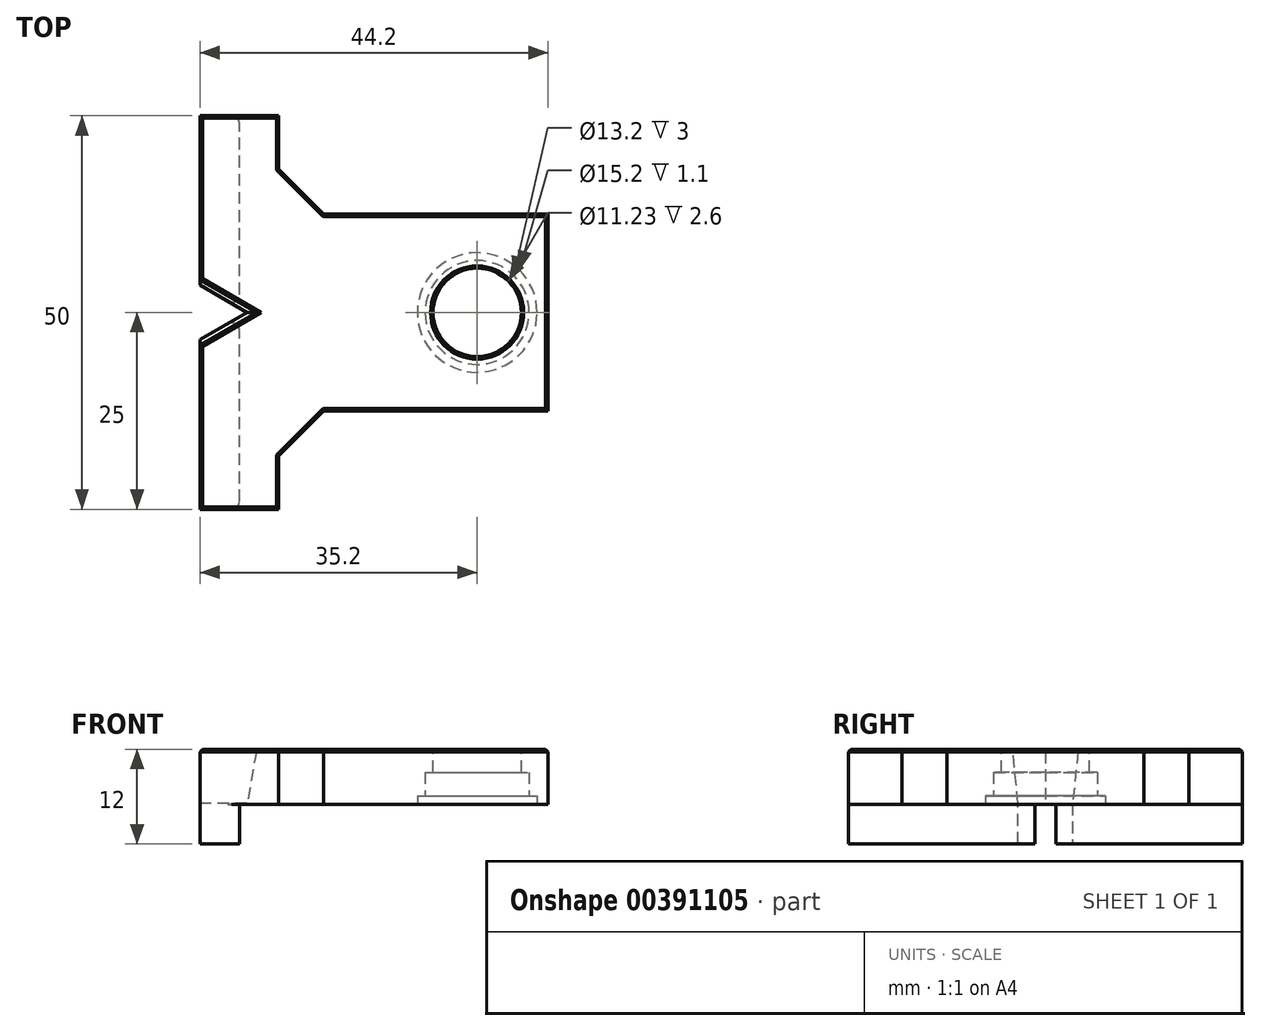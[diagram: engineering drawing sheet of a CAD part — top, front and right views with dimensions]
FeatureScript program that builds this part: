
annotation { "Feature Type Name" : "Feature", "Feature Type Description" : "" }
export const myFeature = defineFeature(function(context is Context, id is Id, definition is map)
    precondition{}
    {
        {
            var Q0;
            Q0=qCreatedBy(makeId("Front.planeOp"),FACE);
            var sketch = newSketch(context, id + "F0", { "sketchPlane" : qUnion([Q0])});
            skLineSegment(sketch, "E0", {"start": v(0, 4) * mm, "end": v(-6.5, 4) * mm});
            skLineSegment(sketch, "E1", {"start": v(-6.5, 4) * mm, "end": v(-6.5, 1) * mm});
            skLineSegment(sketch, "E2", {"start": v(-6.5, 1) * mm, "end": v(-7.5, 1) * mm});
            skLineSegment(sketch, "E3", {"start": v(-7.5, 1) * mm, "end": v(-7.5, 0) * mm});
            skLineSegment(sketch, "E4", {"start": v(-7.5, 0) * mm, "end": v(0, 0) * mm});
            skLineSegment(sketch, "E5", {"start": v(0, 0) * mm, "end": v(0, 4) * mm});
            skLineSegment(sketch, "E6", {"start": v(-5.51, 4) * mm, "end": v(-5.51, 8.08) * mm});
            skLineSegment(sketch, "E7", {"start": v(-5.51, 8.08) * mm, "end": v(0, 8.08) * mm});
            skLineSegment(sketch, "E8", {"start": v(0, 8.08) * mm, "end": v(0, 4) * mm});
            skSolve(sketch);
        }
        {
            var Q0;
            Q0=makeQuery(id+"F0.imprint","IMPRINT",FACE,{"disambiguationData":[TD([[makeQuery(id+"F0.imprint","IMPRINT",EDGE,{"derivedFrom":sQuery(id+"F0.wireOp",EDGE,"E0")}),1.0]])]});
            var Q1;
            {var subQ2=sQuery(id+"F0.wireOp",EDGE,"E6");Q1=makeQuery(id+"F0.imprint","IMPRINT",FACE,{"disambiguationData":[TD([[makeQuery(id+"F0.imprint","IMPRINT",EDGE,{"derivedFrom":subQ2}),-1.0]])]});}
            var Q2;
            Q2=sQuery(id+"F0.wireOp",EDGE,"E5");
            revolve(context, id + "F1", {"entities" : qUnion([Q0, Q1]), "axis" : qUnion([Q2]), "revolveType" : RevolveType.FULL});
        }
        {
            var Q0;
            Q0=qCreatedBy(makeId("Front.planeOp"),FACE);
            var sketch = newSketch(context, id + "F2", { "sketchPlane" : qUnion([Q0])});
            skLineSegment(sketch, "E9", {"start": v(9, 0) * mm, "end": v(-30.2, 0) * mm});
            skLineSegment(sketch, "E10", {"start": v(-35.2, 7) * mm, "end": v(9, 7) * mm});
            skLineSegment(sketch, "E11", {"start": v(9, 7) * mm, "end": v(9, 0) * mm});
            skLineSegment(sketch, "E12", {"start": v(-35.2, 7) * mm, "end": v(-35.2, -5) * mm});
            skLineSegment(sketch, "E13", {"start": v(-35.2, -5) * mm, "end": v(-30.2, -5) * mm});
            skLineSegment(sketch, "E14", {"start": v(-30.2, -5) * mm, "end": v(-30.2, 0) * mm});
            skSolve(sketch);
        }
        {
            var Q0;
            Q0 = qSketchRegion(id + "F2", true);
            extrude(context, id + "F3", {"entities" : qUnion([Q0]), "depth" : 25 * mm, "hasSecondDirection" : true, "secondDirectionOppositeDirection" : true, "secondDirectionDepth" : 25 * mm});
        }
        {
            var Q0;
            Q0=makeQuery(id+"F1.opRevolve","SWEPT_BODY",BODY,{"disambiguationData":[OSD([sQuery(id+"F0.wireOp",EDGE,"E0"),sQuery(id+"F0.wireOp",EDGE,"E1"),sQuery(id+"F0.wireOp",EDGE,"E2"),sQuery(id+"F0.wireOp",EDGE,"E3"),sQuery(id+"F0.wireOp",EDGE,"E4"),sQuery(id+"F0.wireOp",EDGE,"E5"),sQuery(id+"F0.wireOp",EDGE,"E6"),sQuery(id+"F0.wireOp",EDGE,"E7"),sQuery(id+"F0.wireOp",EDGE,"E8")])]});
            var Q1;
            Q1=makeQuery(id+"F3.opExtrude","SWEPT_BODY",BODY,{"disambiguationData":[OSD([sQuery(id+"F2.wireOp",EDGE,"E9"),sQuery(id+"F2.wireOp",EDGE,"qjK4LuHu-fHJy-cj8P-ls5n-CXUVAvU9wVCx"),sQuery(id+"F2.wireOp",EDGE,"mKEJQmDi-ri6G-UNeS-c0yA-2z900LPmcNbM"),sQuery(id+"F2.wireOp",EDGE,"euY9auJU-7oiR-UoH9-VYBM-8SDevPJArw3y"),sQuery(id+"F2.wireOp",EDGE,"E10"),sQuery(id+"F2.wireOp",EDGE,"E11")])]});
            booleanBodies(context, id + "F4", {"operationType" : BooleanOperationType.SUBTRACTION, "tools" : qUnion([Q0]), "targets" : qUnion([Q1]), "offset" : true, "offsetAll" : true, "offsetDistance" : .1 * mm});
        }
        {
            var Q0;
            Q0=qCreatedBy(makeId("Top.planeOp"),FACE);
            var sketch = newSketch(context, id + "F5", { "sketchPlane" : qUnion([Q0])});
            skLineSegment(sketch, "E15", {"start": v(-39.06, 5.7) * mm, "end": v(-29.2, 0) * mm});
            skLineSegment(sketch, "E16", {"start": v(-29.2, 0) * mm, "end": v(-39.06, -5.7) * mm});
            skLineSegment(sketch, "E17", {"start": v(-39.06, -5.7) * mm, "end": v(-39.06, 5.7) * mm});
            skSolve(sketch);
        }
        {
            var Q0;
            Q0=makeQuery(id+"F5.imprint","IMPRINT",FACE,{"disambiguationData":[TD([[makeQuery(id+"F5.imprint","IMPRINT",EDGE,{"derivedFrom":sQuery(id+"F5.wireOp",EDGE,"E15")}),-1.0]])]});
            extrude(context, id + "F6", {"entities" : qUnion([Q0]), "operationType" : NewBodyOperationType.REMOVE, "oppositeDirection" : true, "depth" : 25 * mm, "hasSecondDirection" : true, "secondDirectionOppositeDirection" : false, "secondDirectionDepth" : 25 * mm});
        }
        {
            var Q0;
            Q0=makeQuery(id+"F6.boolean.opBoolean","INTERSECT",EDGE,{"derivedFrom":[makeQuery(id+"F3.opExtrude","SWEPT_FACE",FACE,{"disambiguationData":[OSD([sQuery(id+"F2.wireOp",EDGE,"E10")])]}),makeQuery(id+"F6.opExtrude","SWEPT_FACE",FACE,{"disambiguationData":[OSD([sQuery(id+"F5.wireOp",EDGE,"E16")])]})]});
            var Q1;
            Q1=makeQuery(id+"F6.boolean.opBoolean","INTERSECT",EDGE,{"derivedFrom":[makeQuery(id+"F3.opExtrude","SWEPT_FACE",FACE,{"disambiguationData":[OSD([sQuery(id+"F2.wireOp",EDGE,"E10")])]}),makeQuery(id+"F6.opExtrude","SWEPT_FACE",FACE,{"disambiguationData":[OSD([sQuery(id+"F5.wireOp",EDGE,"E15")])]})]});
            chamfer(context, id + "F7", {"entities" : qUnion([Q0, Q1]), "chamferType" : ChamferType.OFFSET_ANGLE, "width" : 0.6 * mm, "oppositeDirection" : false, "angle" : 85 * degree, "tangentPropagation" : true});
        }
        {
            var Q0;
            {var subQ1=sQuery(id+"F2.wireOp",EDGE,"E14");var subQ3=sQuery(id+"F2.wireOp",EDGE,"E10");var subQ4=makeQuery(id+"F6.opExtrude","SWEPT_FACE",FACE,{"disambiguationData":[OSD([sQuery(id+"F5.wireOp",EDGE,"E15")])]});Q0=makeQuery(id+"F7.opChamfer","BLEND_EDGE",EDGE,{"blendedFrom":[makeQuery(id+"F6.boolean.opBoolean","INTERSECT",EDGE,{"derivedFrom":[makeQuery(id+"F3.opExtrude","SWEPT_FACE",FACE,{"disambiguationData":[OSD([subQ3])]}),subQ4]}),makeQuery(id+"F6.boolean.opBoolean","SPLIT",FACE,{"disambiguationData":[TD([subQ4])],"derivedFrom":makeQuery(id+"F3.opExtrude","SWEPT_FACE",FACE,{"disambiguationData":[OSD([subQ1])]})})],"blendedInto":[makeQuery(id+"F6.boolean.opBoolean","SPLIT",FACE,{"disambiguationData":[TD([subQ4])],"derivedFrom":makeQuery(id+"F3.opExtrude","SWEPT_FACE",FACE,{"disambiguationData":[OSD([subQ1])]})})]});}
            var Q1;
            {var subQ1=sQuery(id+"F2.wireOp",EDGE,"E14");var subQ3=sQuery(id+"F2.wireOp",EDGE,"E10");var subQ4=makeQuery(id+"F6.opExtrude","SWEPT_FACE",FACE,{"disambiguationData":[OSD([sQuery(id+"F5.wireOp",EDGE,"E16")])]});Q1=makeQuery(id+"F7.opChamfer","BLEND_EDGE",EDGE,{"blendedFrom":[makeQuery(id+"F6.boolean.opBoolean","INTERSECT",EDGE,{"derivedFrom":[makeQuery(id+"F3.opExtrude","SWEPT_FACE",FACE,{"disambiguationData":[OSD([subQ3])]}),subQ4]}),makeQuery(id+"F6.boolean.opBoolean","SPLIT",FACE,{"disambiguationData":[TD([subQ4])],"derivedFrom":makeQuery(id+"F3.opExtrude","SWEPT_FACE",FACE,{"disambiguationData":[OSD([subQ1])]})})],"blendedInto":[makeQuery(id+"F6.boolean.opBoolean","SPLIT",FACE,{"disambiguationData":[TD([subQ4])],"derivedFrom":makeQuery(id+"F3.opExtrude","SWEPT_FACE",FACE,{"disambiguationData":[OSD([subQ1])]})})]});}
            var Q2;
            Q2=makeQuery(id+"F3.opExtrude","CAP_EDGE",EDGE,{"disambiguationData":[OSD([sQuery(id+"F2.wireOp",EDGE,"E14")])],"isStart":false});
            var Q3;
            Q3=makeQuery(id+"F3.opExtrude","CAP_EDGE",EDGE,{"disambiguationData":[OSD([sQuery(id+"F2.wireOp",EDGE,"E14")])],"isStart":true});
            var Q4;
            Q4=makeQuery(id+"F6.boolean.opBoolean","INTERSECT",EDGE,{"derivedFrom":[makeQuery(id+"F3.opExtrude","SWEPT_FACE",FACE,{"disambiguationData":[OSD([sQuery(id+"F2.wireOp",EDGE,"E14")])]}),makeQuery(id+"F6.opExtrude","SWEPT_FACE",FACE,{"disambiguationData":[OSD([sQuery(id+"F5.wireOp",EDGE,"E16")])]})]});
            var Q5;
            Q5=makeQuery(id+"F6.boolean.opBoolean","INTERSECT",EDGE,{"derivedFrom":[makeQuery(id+"F3.opExtrude","SWEPT_FACE",FACE,{"disambiguationData":[OSD([sQuery(id+"F2.wireOp",EDGE,"E14")])]}),makeQuery(id+"F6.opExtrude","SWEPT_FACE",FACE,{"disambiguationData":[OSD([sQuery(id+"F5.wireOp",EDGE,"E15")])]})]});
            fillet(context, id + "F8", {"entities" : qUnion([Q0, Q1, Q2, Q3, Q4, Q5]), "radius" : 1 * mm, "tangentPropagation" : true, "allowEdgeOverflow" : false});
        }
        {
            var Q0;
            Q0=makeQuery(id+"F3.opExtrude","SWEPT_FACE",FACE,{"disambiguationData":[OSD([sQuery(id+"F2.wireOp",EDGE,"E10")])]});
            var sketch = newSketch(context, id + "F9", { "sketchPlane" : qUnion([Q0])});
            skLineSegment(sketch, "E18", {"start": v(-25.2, 33.97) * mm, "end": v(-25.2, 18.22) * mm});
            skLineSegment(sketch, "E19", {"start": v(-25.2, 18.22) * mm, "end": v(-19.48, 12.5) * mm});
            skLineSegment(sketch, "E20", {"start": v(-19.48, 12.5) * mm, "end": v(17.82, 12.5) * mm});
            skLineSegment(sketch, "E21", {"start": v(17.82, 12.5) * mm, "end": v(17.82, -12.5) * mm});
            skLineSegment(sketch, "E22", {"start": v(17.82, -12.5) * mm, "end": v(-19.48, -12.5) * mm});
            skLineSegment(sketch, "E23", {"start": v(-19.48, -12.5) * mm, "end": v(-25.2, -18.22) * mm});
            skLineSegment(sketch, "E24", {"start": v(-25.2, -18.22) * mm, "end": v(-25.2, -38.35) * mm});
            skLineSegment(sketch, "E25", {"start": v(-25.2, -38.35) * mm, "end": v(-40.1, -38.35) * mm});
            skLineSegment(sketch, "E26", {"start": v(-40.1, -38.35) * mm, "end": v(-40.1, 33.97) * mm});
            skLineSegment(sketch, "E27", {"start": v(-40.1, 33.97) * mm, "end": v(-25.2, 33.97) * mm});
            skSolve(sketch);
        }
        {
            var Q0;
            {var subQ19=sQuery(id+"F9.wireOp",EDGE,"E19");Q0=makeQuery(id+"F9.imprint","IMPRINT",FACE,{"disambiguationData":[TD([[makeQuery(id+"F9.imprint","IMPRINT",EDGE,{"derivedFrom":subQ19}),-1.0]])]});}
            var Q1;
            {var subQ0=sQuery(id+"F9.wireOp",EDGE,"E21");Q1=makeQuery(id+"F9.imprint","IMPRINT",FACE,{"disambiguationData":[TD([[makeQuery(id+"F9.imprint","IMPRINT",EDGE,{"derivedFrom":subQ0}),-1.0]])]});}
            var Q2;
            {var subQ17=sQuery(id+"F9.wireOp",EDGE,"E25");Q2=makeQuery(id+"F9.imprint","IMPRINT",FACE,{"disambiguationData":[TD([[makeQuery(id+"F9.imprint","IMPRINT",EDGE,{"derivedFrom":subQ17}),-1.0]])]});}
            extrude(context, id + "F10", {"entities" : qUnion([Q0, Q1, Q2]), "oppositeDirection" : true, "depth" : 25 * mm});
        }
        {
            var Q0;
            Q0=makeQuery(id+"F10.opExtrude","SWEPT_BODY",BODY,{"disambiguationData":[OSD([sQuery(id+"F0.wireOp",EDGE,"E6"),sQuery(id+"F2.wireOp",EDGE,"E10"),sQuery(id+"F9.wireOp",EDGE,"E18"),sQuery(id+"F9.wireOp",EDGE,"E19"),sQuery(id+"F9.wireOp",EDGE,"E20"),sQuery(id+"F9.wireOp",EDGE,"E21"),sQuery(id+"F9.wireOp",EDGE,"E22"),sQuery(id+"F9.wireOp",EDGE,"E23"),sQuery(id+"F9.wireOp",EDGE,"E24"),sQuery(id+"F9.wireOp",EDGE,"E25"),sQuery(id+"F9.wireOp",EDGE,"E26"),sQuery(id+"F9.wireOp",EDGE,"E27")])]});
            var Q1;
            Q1=makeQuery(id+"F3.opExtrude","SWEPT_BODY",BODY,{"disambiguationData":[OSD([sQuery(id+"F2.wireOp",EDGE,"E9"),sQuery(id+"F2.wireOp",EDGE,"E10"),sQuery(id+"F2.wireOp",EDGE,"E11"),sQuery(id+"F2.wireOp",EDGE,"E12"),sQuery(id+"F2.wireOp",EDGE,"E13"),sQuery(id+"F2.wireOp",EDGE,"E14")])]});
            booleanBodies(context, id + "F11", {"operationType" : BooleanOperationType.INTERSECTION, "tools" : qUnion([Q0, Q1])});
        }
        {
            var Q0;
            Q0=makeQuery(id+"F10.opExtrude","CAP_FACE",FACE,{"disambiguationData":[OSD([sQuery(id+"F0.wireOp",EDGE,"E6"),sQuery(id+"F2.wireOp",EDGE,"E10"),sQuery(id+"F9.wireOp",EDGE,"E18"),sQuery(id+"F9.wireOp",EDGE,"E19"),sQuery(id+"F9.wireOp",EDGE,"E20"),sQuery(id+"F9.wireOp",EDGE,"E21"),sQuery(id+"F9.wireOp",EDGE,"E22"),sQuery(id+"F9.wireOp",EDGE,"E23"),sQuery(id+"F9.wireOp",EDGE,"E24"),sQuery(id+"F9.wireOp",EDGE,"E25"),sQuery(id+"F9.wireOp",EDGE,"E26"),sQuery(id+"F9.wireOp",EDGE,"E27")])],"isStart":true});
            chamfer(context, id + "F12", {"entities" : qUnion([Q0]), "width" : 0.3 * mm, "tangentPropagation" : true});
        }
    });
